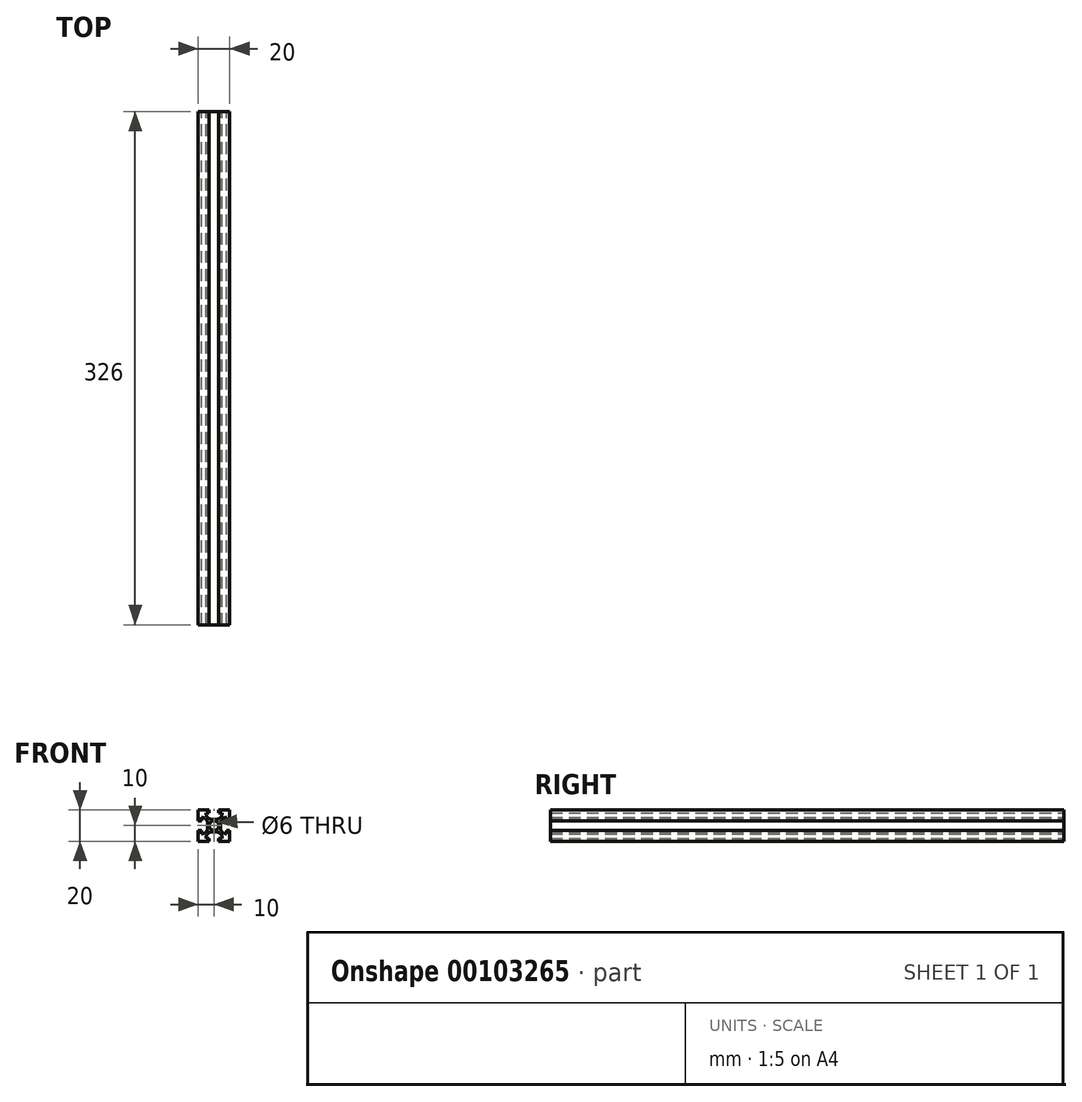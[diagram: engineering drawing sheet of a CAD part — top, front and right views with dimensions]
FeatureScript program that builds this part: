
annotation { "Feature Type Name" : "Feature", "Feature Type Description" : "" }
export const myFeature = defineFeature(function(context is Context, id is Id, definition is map)
    precondition{}
    {
        {
            var Q0;
            Q0=qCreatedBy(makeId("Front.planeOp"),FACE);
            var sketch = newSketch(context, id + "F0", { "sketchPlane" : qUnion([Q0])});
            skCircle(sketch, "E0", {"center": v(0, 0) * mm, "radius": 3 * mm});
            skLineSegment(sketch, "E1.left", {"start": v(3, 8) * mm, "end": v(3, 10) * mm});
            skLineSegment(sketch, "E2", {"start": v(3, 10) * mm, "end": v(10, 10) * mm});
            skLineSegment(sketch, "E3", {"start": v(3, 8) * mm, "end": v(5.19, 8) * mm});
            skLineSegment(sketch, "E4", {"start": v(0, 4) * mm, "end": v(1.21, 4) * mm});
            skLineSegment(sketch, "E5", {"start": v(0, 0) * mm, "end": v(10, 10) * mm, "construction": true});
            skArc(sketch, "E6", {"start": v(1.21, 4) * mm, "mid": v(4.03, 5.17) * mm, "end": v(5.19, 8) * mm});
            skLineSegment(sketch, "E7.MirrorCS", {"start": v(10, 3) * mm, "end": v(10, 10) * mm});
            skLineSegment(sketch, "E8.MirrorCS", {"start": v(8, 3) * mm, "end": v(10, 3) * mm});
            skLineSegment(sketch, "E9.MirrorCS", {"start": v(8, 3) * mm, "end": v(8, 5.19) * mm});
            skArc(sketch, "E10.MirrorCS", {"start": v(4, 1.21) * mm, "mid": v(5.17, 4.03) * mm, "end": v(8, 5.19) * mm});
            skLineSegment(sketch, "E11.MirrorCS", {"start": v(4, 0) * mm, "end": v(4, 1.21) * mm});
            skLineSegment(sketch, "E12.MirrorCS", {"start": v(-3, 8) * mm, "end": v(-3, 10) * mm});
            skLineSegment(sketch, "E13.MirrorCS", {"start": v(-3, 10) * mm, "end": v(-10, 10) * mm});
            skArc(sketch, "E14.MirrorCS", {"start": v(-4, 1.21) * mm, "mid": v(-5.17, 4.03) * mm, "end": v(-8, 5.19) * mm});
            skLineSegment(sketch, "E15.MirrorCS", {"start": v(-4, 0) * mm, "end": v(-4, 1.21) * mm});
            skLineSegment(sketch, "E16.MirrorCS", {"start": v(0, 4) * mm, "end": v(-1.21, 4) * mm});
            skLineSegment(sketch, "E17.MirrorCS", {"start": v(0, 0) * mm, "end": v(-10, 10) * mm, "construction": true});
            skLineSegment(sketch, "E18.MirrorCS", {"start": v(-8, 3) * mm, "end": v(-10, 3) * mm});
            skLineSegment(sketch, "E19.MirrorCS", {"start": v(-8, 3) * mm, "end": v(-8, 5.19) * mm});
            skLineSegment(sketch, "E20.MirrorCS", {"start": v(-10, 3) * mm, "end": v(-10, 10) * mm});
            skLineSegment(sketch, "E21.MirrorCS", {"start": v(-3, 8) * mm, "end": v(-5.19, 8) * mm});
            skArc(sketch, "E22.MirrorCS", {"start": v(-1.21, 4) * mm, "mid": v(-4.03, 5.17) * mm, "end": v(-5.19, 8) * mm});
            skLineSegment(sketch, "E23.MirrorCS", {"start": v(0, -4) * mm, "end": v(-1.21, -4) * mm});
            skLineSegment(sketch, "E24.MirrorCS", {"start": v(-8, -3) * mm, "end": v(-10, -3) * mm});
            skLineSegment(sketch, "E25.MirrorCS", {"start": v(-10, -3) * mm, "end": v(-10, -10) * mm});
            skArc(sketch, "E26.MirrorCS", {"start": v(-1.21, -4) * mm, "mid": v(-4.03, -5.17) * mm, "end": v(-5.19, -8) * mm});
            skLineSegment(sketch, "E27.MirrorCS", {"start": v(-3, -8) * mm, "end": v(-3, -10) * mm});
            skLineSegment(sketch, "E28.MirrorCS", {"start": v(4, 0) * mm, "end": v(4, -1.21) * mm});
            skArc(sketch, "E29.MirrorCS", {"start": v(4, -1.21) * mm, "mid": v(5.17, -4.03) * mm, "end": v(8, -5.19) * mm});
            skLineSegment(sketch, "E30.MirrorCS", {"start": v(8, -3) * mm, "end": v(8, -5.19) * mm});
            skLineSegment(sketch, "E31.MirrorCS", {"start": v(8, -3) * mm, "end": v(10, -3) * mm});
            skLineSegment(sketch, "E32.MirrorCS", {"start": v(10, -3) * mm, "end": v(10, -10) * mm});
            skArc(sketch, "E33.MirrorCS", {"start": v(1.21, -4) * mm, "mid": v(4.03, -5.17) * mm, "end": v(5.19, -8) * mm});
            skLineSegment(sketch, "E34.MirrorCS", {"start": v(0, 0) * mm, "end": v(10, -10) * mm, "construction": true});
            skLineSegment(sketch, "E35.MirrorCS", {"start": v(0, -4) * mm, "end": v(1.21, -4) * mm});
            skLineSegment(sketch, "E36.MirrorCS", {"start": v(3, -8) * mm, "end": v(5.19, -8) * mm});
            skLineSegment(sketch, "E37.MirrorCS", {"start": v(3, -8) * mm, "end": v(3, -10) * mm});
            skLineSegment(sketch, "E38.MirrorCS", {"start": v(0, 0) * mm, "end": v(-10, -10) * mm, "construction": true});
            skArc(sketch, "E39.MirrorCS", {"start": v(-4, -1.21) * mm, "mid": v(-5.17, -4.03) * mm, "end": v(-8, -5.19) * mm});
            skLineSegment(sketch, "E40.MirrorCS", {"start": v(-3, -10) * mm, "end": v(-10, -10) * mm});
            skLineSegment(sketch, "E41.MirrorCS", {"start": v(3, -10) * mm, "end": v(10, -10) * mm});
            skLineSegment(sketch, "E42.MirrorCS", {"start": v(-3, -8) * mm, "end": v(-5.19, -8) * mm});
            skLineSegment(sketch, "E43.MirrorCS", {"start": v(-4, 0) * mm, "end": v(-4, -1.21) * mm});
            skLineSegment(sketch, "E44.MirrorCS", {"start": v(-8, -3) * mm, "end": v(-8, -5.19) * mm});
            skSolve(sketch);
        }
        {
            var Q0;
            Q0=makeQuery(id+"F0.imprint","IMPRINT",FACE,{"disambiguationData":[TD([[makeQuery(id+"F0.imprint","IMPRINT",EDGE,{"derivedFrom":sQuery(id+"F0.wireOp",EDGE,"E0")}),-1.0]])]});
            extrude(context, id + "F1", {"entities" : qUnion([Q0]), "depth" : (326 / 2) * mm, "hasSecondDirection" : true, "secondDirectionOppositeDirection" : true, "secondDirectionDepth" : (326 / 2) * mm});
        }
    });
